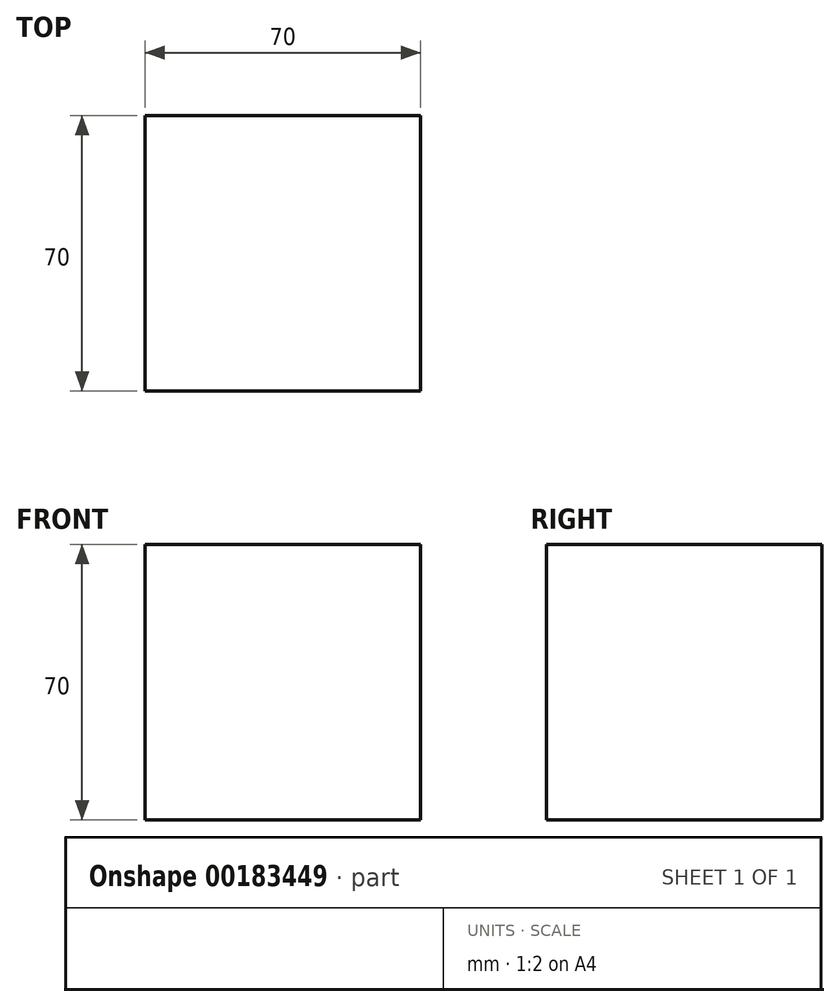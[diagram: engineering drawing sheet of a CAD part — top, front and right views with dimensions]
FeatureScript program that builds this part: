
annotation { "Feature Type Name" : "Feature", "Feature Type Description" : "" }
export const myFeature = defineFeature(function(context is Context, id is Id, definition is map)
    precondition{}
    {
        {
            var Q0;
            Q0=qCreatedBy(makeId("Front.planeOp"),FACE);
            var sketch = newSketch(context, id + "F0", { "sketchPlane" : qUnion([Q0])});
            skLineSegment(sketch, "E0.bottom", {"start": v(-40.76, 30.77) * mm, "end": v(29.24, 30.77) * mm});
            skLineSegment(sketch, "E0.top", {"start": v(-40.76, -39.23) * mm, "end": v(29.24, -39.23) * mm});
            skLineSegment(sketch, "E0.left", {"start": v(-40.76, 30.77) * mm, "end": v(-40.76, -39.23) * mm});
            skLineSegment(sketch, "E0.right", {"start": v(29.24, 30.77) * mm, "end": v(29.24, -39.23) * mm});
            skSolve(sketch);
        }
        {
            var Q0;
            Q0 = qSketchRegion(id + "F0", true);
            extrude(context, id + "F1", {"entities" : qUnion([Q0]), "depth" : 70 * mm});
        }
    });
